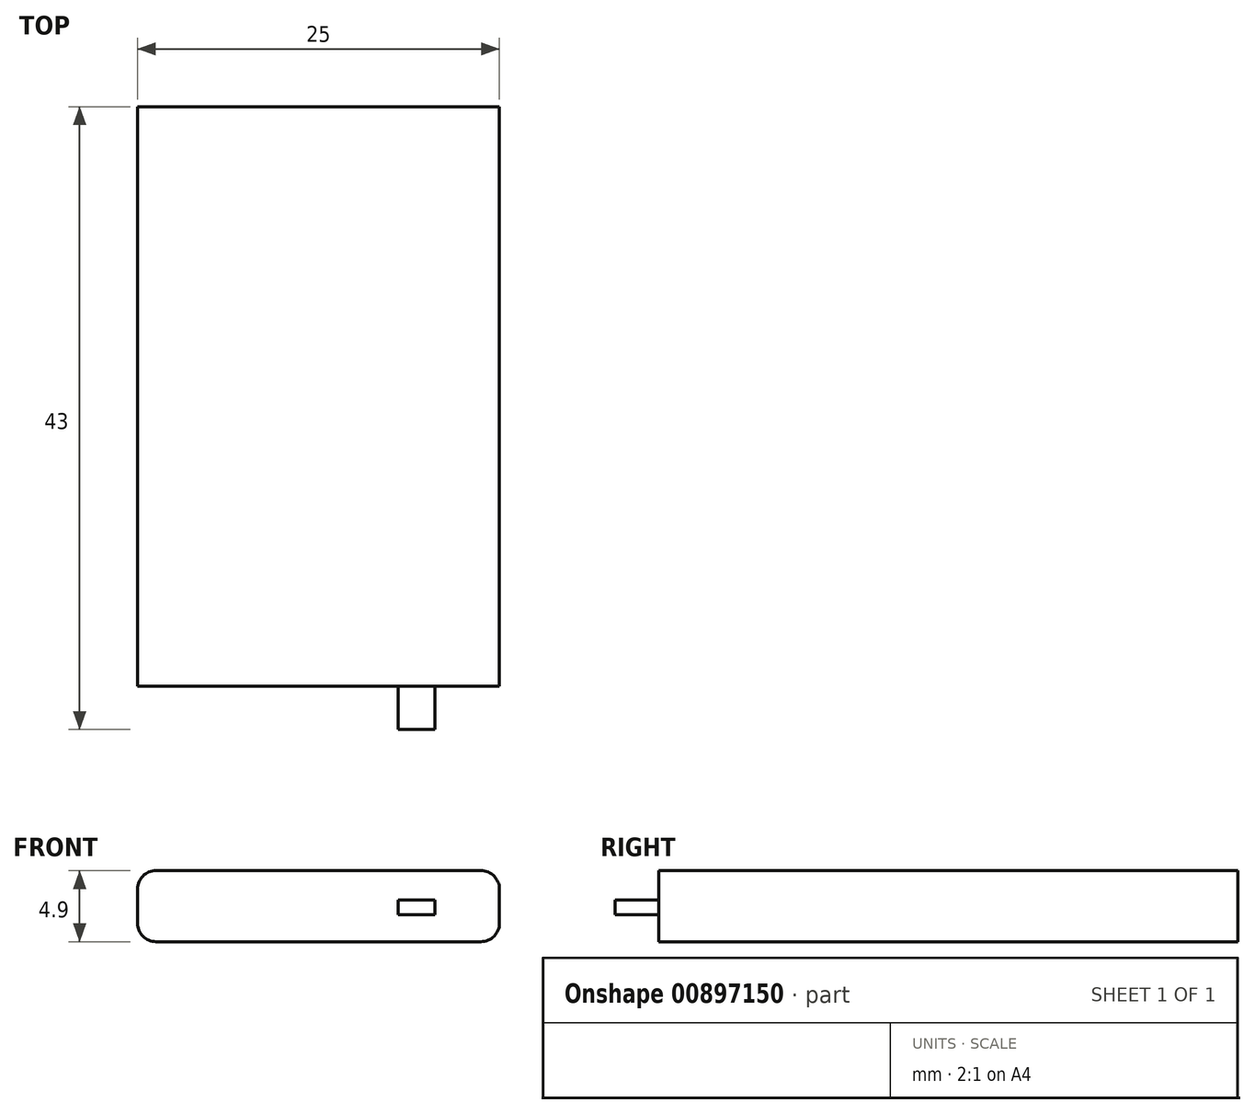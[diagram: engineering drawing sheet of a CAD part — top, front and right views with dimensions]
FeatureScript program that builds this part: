
annotation { "Feature Type Name" : "Feature", "Feature Type Description" : "" }
export const myFeature = defineFeature(function(context is Context, id is Id, definition is map)
    precondition{}
    {
        {
            var Q0;
            Q0=qCreatedBy(makeId("Top.planeOp"),FACE);
            var sketch = newSketch(context, id + "F0", { "sketchPlane" : qUnion([Q0])});
            skLineSegment(sketch, "E0.bottom", {"start": v(12.5, 20) * mm, "end": v(-12.5, 20) * mm});
            skLineSegment(sketch, "E0.top", {"start": v(12.5, -20) * mm, "end": v(-12.5, -20) * mm});
            skLineSegment(sketch, "E0.left", {"start": v(12.5, 20) * mm, "end": v(12.5, -20) * mm});
            skLineSegment(sketch, "E0.right", {"start": v(-12.5, 20) * mm, "end": v(-12.5, -20) * mm});
            skPoint(sketch, "E0.middle", {"position": v(0, 0) * mm});
            skSolve(sketch);
        }
        {
            var Q0;
            Q0 = qSketchRegion(id + "F0", true);
            extrude(context, id + "F1", {"entities" : qUnion([Q0]), "depth" : 4.9 * mm, "offsetDistance" : 25.4 * mm});
        }
        {
            var Q0;
            Q0=makeQuery(id+"F1.opExtrude","CAP_EDGE",EDGE,{"disambiguationData":[OSD([sQuery(id+"F0.wireOp",EDGE,"E0.right")])],"isStart":false});
            var Q1;
            Q1=makeQuery(id+"F1.opExtrude","CAP_EDGE",EDGE,{"disambiguationData":[OSD([sQuery(id+"F0.wireOp",EDGE,"E0.left")])],"isStart":false});
            var Q2;
            Q2=makeQuery(id+"F1.opExtrude","CAP_EDGE",EDGE,{"disambiguationData":[OSD([sQuery(id+"F0.wireOp",EDGE,"E0.left")])],"isStart":true});
            var Q3;
            Q3=makeQuery(id+"F1.opExtrude","CAP_EDGE",EDGE,{"disambiguationData":[OSD([sQuery(id+"F0.wireOp",EDGE,"E0.right")])],"isStart":true});
            fillet(context, id + "F2", {"entities" : qUnion([Q0, Q1, Q2, Q3]), "radius" : 1.27 * mm, "tangentPropagation" : true, "allowEdgeOverflow" : false});
        }
        {
            var Q0;
            Q0=makeQuery(id+"F1.opExtrude","SWEPT_FACE",FACE,{"disambiguationData":[OSD([sQuery(id+"F0.wireOp",EDGE,"E0.top")])]});
            var sketch = newSketch(context, id + "F3", { "sketchPlane" : qUnion([Q0])});
            skLineSegment(sketch, "E1.bottom", {"start": v(8.06, 1.85) * mm, "end": v(5.52, 1.85) * mm});
            skLineSegment(sketch, "E1.top", {"start": v(8.06, 2.87) * mm, "end": v(5.52, 2.87) * mm});
            skLineSegment(sketch, "E1.left", {"start": v(8.06, 1.85) * mm, "end": v(8.06, 2.87) * mm});
            skLineSegment(sketch, "E1.right", {"start": v(5.52, 1.85) * mm, "end": v(5.52, 2.87) * mm});
            skPoint(sketch, "E1.middle", {"position": v(6.79, 2.36) * mm});
            skSolve(sketch);
        }
        {
            var Q0;
            Q0 = qSketchRegion(id + "F3", true);
            extrude(context, id + "F4", {"entities" : qUnion([Q0]), "operationType" : NewBodyOperationType.ADD, "depth" : 3 * mm, "offsetDistance" : 25.4 * mm});
        }
    });
